# Revit family: LAMP_ARO DECO
name_source: partatom
category: Modelos genéricos
revit_build: Autodesk Revit 2015 (Build: 20140606_1530(x64)
units: mm (PartAtom-declared; Revit-internal decimal feet)

## types (3) — shared parameters
Comentarios de tipo = Availability of switching between accessories through visibility parameters when placed in a project.
Diameter = 226 mm  [stored 0.74147 ft]
Fabricante = LAMP
Grosor aro = 2 mm  [stored 0.00656168 ft]
Last update = 22/05/2020
Luminaire type = Accessory
Manufacturer URL = http://www.lamp.es
Manufacturer country = Spain
Manufacturer name = LAMP
Model explanation = Availability of switching between accessories through visibility parameters when placed in a project.
Product URL = https://www.lamp.es
Product datasheet = https://www.lamp.es
Weight = 0.10 kg

## per-type parameters (varying)
| type | Descripción | Finish | Material Aro | Modelo | Product code |
| WHITE | KOMBIC ACC. DECO RING WH. | Shiny white | LAMP_PC Kombic Aro BL | RIRD240W
RIRD240W
RIRD240W | RIRD240W
RIRD240W
RIRD240W |
| GREY | KOMBIC ACC. DECO RING GR. | Gloss grey | LAMP_PC Kombic Aro GR | RIRD240G | RIRD240G |
| BLACK | KOMBIC ACC. DECO RING BL. | RAL 9011 | LAMP_PC Kombic Aro ng | RIRD240B | RIRD240B |

note: [stored X ft] marks values corroborated as IEEE doubles in the binary element streams (Revit-internal decimal feet)
